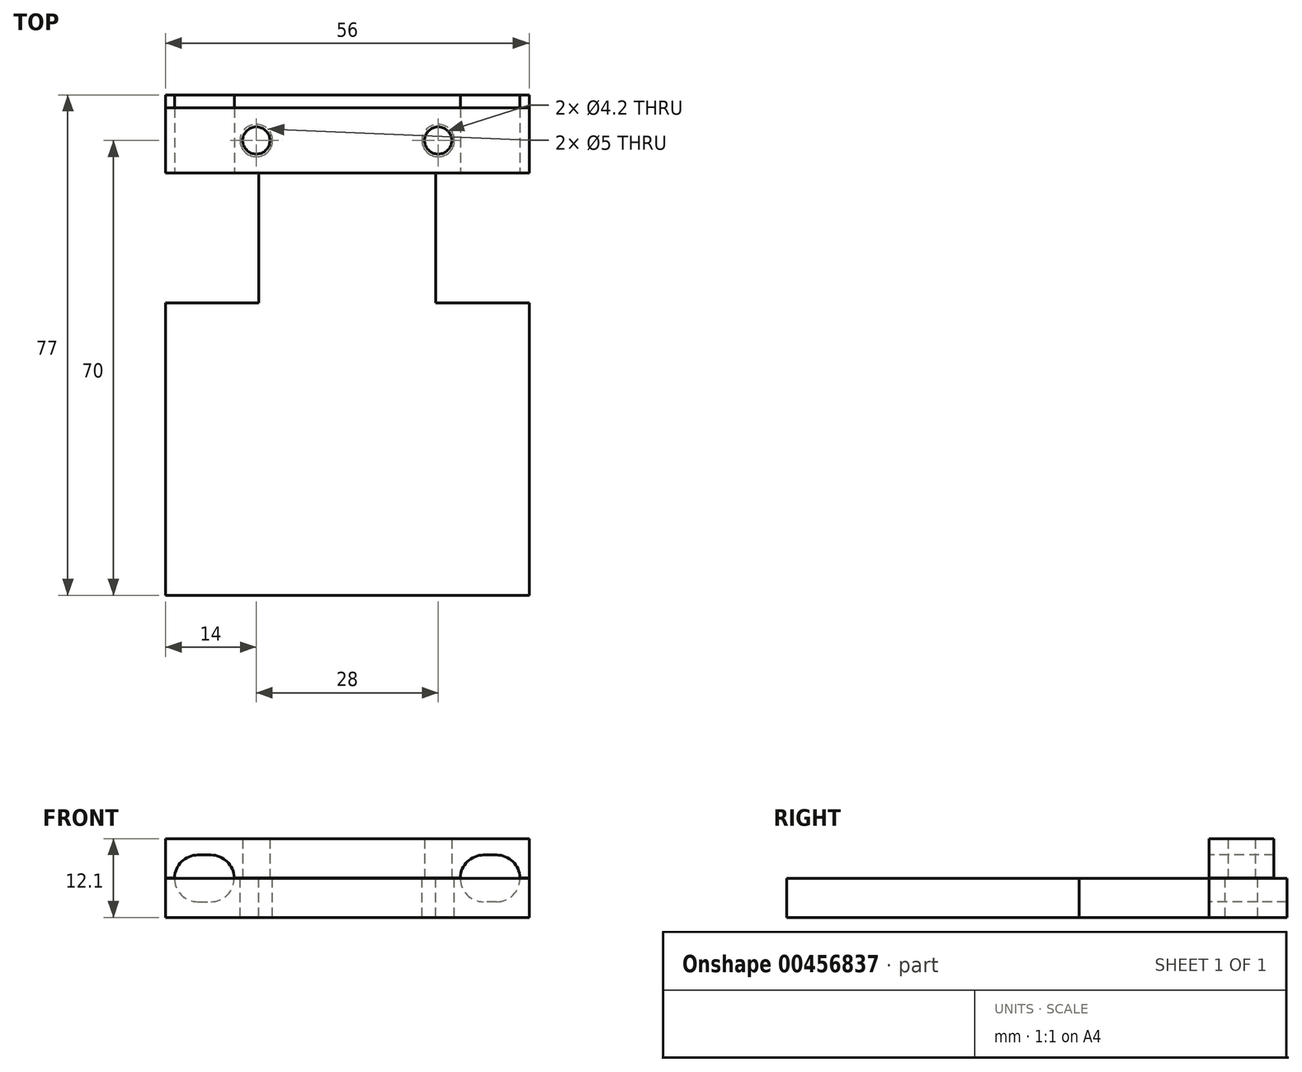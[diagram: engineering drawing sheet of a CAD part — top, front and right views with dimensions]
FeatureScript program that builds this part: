
annotation { "Feature Type Name" : "Feature", "Feature Type Description" : "" }
export const myFeature = defineFeature(function(context is Context, id is Id, definition is map)
    precondition{}
    {
        {
            var Q0;
            Q0=qCreatedBy(makeId("Front.planeOp"),FACE);
            var sketch = newSketch(context, id + "F0", { "sketchPlane" : qUnion([Q0])});
            skLineSegment(sketch, "E0", {"start": v(0, 0) * mm, "end": v(17.4, 0) * mm});
            skLineSegment(sketch, "E1", {"start": v(17.4, 0) * mm, "end": v(17.4, -6) * mm});
            skLineSegment(sketch, "E2", {"start": v(-17.4, -6) * mm, "end": v(-17.4, 0) * mm});
            skLineSegment(sketch, "E3", {"start": v(-17.4, 0) * mm, "end": v(0, 0) * mm});
            skCircle(sketch, "E4", {"center": v(21, 0) * mm, "radius": 3.6 * mm});
            skCircle(sketch, "E5", {"center": v(-21, 0) * mm, "radius": 3.6 * mm});
            skLineSegment(sketch, "E6", {"start": v(24.6, 0) * mm, "end": v(28, 0) * mm});
            skLineSegment(sketch, "E7", {"start": v(28, 0) * mm, "end": v(28, -6) * mm});
            skLineSegment(sketch, "E8", {"start": v(28, -6) * mm, "end": v(17.4, -6) * mm});
            skLineSegment(sketch, "E9", {"start": v(-24.6, 0) * mm, "end": v(-28, 0) * mm});
            skLineSegment(sketch, "E10", {"start": v(-28, 0) * mm, "end": v(-28, -6) * mm});
            skLineSegment(sketch, "E11", {"start": v(-28, -6) * mm, "end": v(-17.4, -6) * mm});
            skLineSegment(sketch, "E12", {"start": v(0, 0) * mm, "end": v(0, -6) * mm});
            skLineSegment(sketch, "E13", {"start": v(-28, 0) * mm, "end": v(-28, 6.1) * mm});
            skLineSegment(sketch, "E14", {"start": v(-28, 6.1) * mm, "end": v(28, 6.1) * mm});
            skLineSegment(sketch, "E15", {"start": v(28, 6.1) * mm, "end": v(28, 0) * mm});
            skLineSegment(sketch, "E16", {"start": v(-17.4, -6) * mm, "end": v(17.4, -6) * mm});
            skLineSegment(sketch, "E17", {"start": v(21, 0) * mm, "end": v(23, 0) * mm, "construction": true});
            skLineSegment(sketch, "E18", {"start": v(-21, 0) * mm, "end": v(-23, 0) * mm, "construction": true});
            skCircle(sketch, "E19", {"center": v(-23, 0) * mm, "radius": 3.6 * mm});
            skCircle(sketch, "E20", {"center": v(23, 0) * mm, "radius": 3.6 * mm});
            skLineSegment(sketch, "E21", {"start": v(-21, 3.6) * mm, "end": v(-23, 3.6) * mm});
            skLineSegment(sketch, "E22", {"start": v(-23, -3.6) * mm, "end": v(-21, -3.6) * mm});
            skLineSegment(sketch, "E23", {"start": v(23, 3.6) * mm, "end": v(21, 3.6) * mm});
            skLineSegment(sketch, "E24", {"start": v(23, -3.6) * mm, "end": v(21, -3.6) * mm});
            skLineSegment(sketch, "E25", {"start": v(-13.6, -6) * mm, "end": v(-13.6, 0) * mm});
            skLineSegment(sketch, "E26", {"start": v(13.6, -6) * mm, "end": v(13.6, 0) * mm});
            skPoint(sketch, "E27.orphan", {"position": v(13.6, -6) * mm});
            skLineSegment(sketch, "E28", {"start": v(-28, 0.1) * mm, "end": v(28, 0.1) * mm});
            skSolve(sketch);
        }
        {
            var Q0;
            {var subQ0=sQuery(id+"F0.wireOp",EDGE,"E0");Q0=makeQuery(id+"F0.imprint","IMPRINT",FACE,{"disambiguationData":[TD([[makeQuery(id+"F0.imprint","IMPRINT",EDGE,{"derivedFrom":subQ0}),-1.0]])]});}
            var Q1;
            {var subQ0=sQuery(id+"F0.wireOp",EDGE,"E3");Q1=makeQuery(id+"F0.imprint","IMPRINT",FACE,{"disambiguationData":[TD([[makeQuery(id+"F0.imprint","IMPRINT",EDGE,{"derivedFrom":subQ0}),-1.0]])]});}
            var Q2;
            {var subQ0=sQuery(id+"F0.wireOp",EDGE,"E10");Q2=makeQuery(id+"F0.imprint","IMPRINT",FACE,{"disambiguationData":[TD([[makeQuery(id+"F0.imprint","IMPRINT",EDGE,{"derivedFrom":subQ0}),1.0]])]});}
            var Q3;
            {var subQ0=sQuery(id+"F0.wireOp",EDGE,"E7");Q3=makeQuery(id+"F0.imprint","IMPRINT",FACE,{"disambiguationData":[TD([[makeQuery(id+"F0.imprint","IMPRINT",EDGE,{"derivedFrom":subQ0}),-1.0]])]});}
            extrude(context, id + "F1", {"entities" : qUnion([Q0, Q1, Q2, Q3]), "oppositeDirection" : true, "depth" : 12 * mm, "offsetDistance" : 25 * mm});
        }
        {
            var Q0;
            Q0=makeQuery(id+"F1.opExtrude","SWEPT_FACE",FACE,{"disambiguationData":[OSD([sQuery(id+"F0.wireOp",EDGE,"E0"),sQuery(id+"F0.wireOp",EDGE,"E3")])]});
            var sketch = newSketch(context, id + "F2", { "sketchPlane" : qUnion([Q0])});
            skLineSegment(sketch, "E29", {"start": v(0, -50) * mm, "end": v(0, 0) * mm, "construction": true});
            skCircle(sketch, "E30", {"center": v(0, -50) * mm, "radius": 13.6 * mm});
            skCircle(sketch, "E31", {"center": v(0, -50) * mm, "radius": 11 * mm});
            skLineSegment(sketch, "E32", {"start": v(0, -50) * mm, "end": v(0, -63.6) * mm, "construction": true});
            skPoint(sketch, "E33.orphan", {"position": v(0, -63.6) * mm});
            skLineSegment(sketch, "E34", {"start": v(-13.6, -50) * mm, "end": v(-13.6, 0) * mm});
            skLineSegment(sketch, "E35", {"start": v(-13.6, 0) * mm, "end": v(0, 0) * mm});
            skLineSegment(sketch, "E36", {"start": v(13.6, 0) * mm, "end": v(13.6, -50) * mm});
            skCircle(sketch, "E37", {"center": v(-6, -50) * mm, "radius": 2.5 * mm});
            skCircle(sketch, "E38", {"center": v(6, -50) * mm, "radius": 2.5 * mm});
            skCircle(sketch, "E39", {"center": v(-6, -50) * mm, "radius": 2.17 * mm});
            skCircle(sketch, "E40", {"center": v(6, -50) * mm, "radius": 2.17 * mm});
            skLineSegment(sketch, "E41.bottom", {"start": v(-9.6, -5) * mm, "end": v(-4.6, -5) * mm});
            skLineSegment(sketch, "E41.top", {"start": v(-9.6, -32.5) * mm, "end": v(-4.6, -32.5) * mm});
            skLineSegment(sketch, "E41.left", {"start": v(-9.6, -5) * mm, "end": v(-9.6, -32.5) * mm});
            skLineSegment(sketch, "E41.right", {"start": v(-4.6, -5) * mm, "end": v(-4.6, -32.5) * mm});
            skLineSegment(sketch, "E42.bottom", {"start": v(4.6, -5) * mm, "end": v(9.6, -5) * mm});
            skLineSegment(sketch, "E42.top", {"start": v(4.6, -32.5) * mm, "end": v(9.6, -32.5) * mm});
            skLineSegment(sketch, "E42.left", {"start": v(4.6, -5) * mm, "end": v(4.6, -32.5) * mm});
            skLineSegment(sketch, "E42.right", {"start": v(9.6, -5) * mm, "end": v(9.6, -32.5) * mm});
            skSolve(sketch);
        }
        {
            var Q0;
            Q0=qCreatedBy(makeId("Top.planeOp"),FACE);
            var sketch = newSketch(context, id + "F3", { "sketchPlane" : qUnion([Q0])});
            skLineSegment(sketch, "E43", {"start": v(0, 0) * mm, "end": v(0, 5) * mm, "construction": true});
            skLineSegment(sketch, "E44", {"start": v(0, 5) * mm, "end": v(14, 5) * mm, "construction": true});
            skLineSegment(sketch, "E45", {"start": v(0, 5) * mm, "end": v(-14, 5) * mm, "construction": true});
            skCircle(sketch, "E46", {"center": v(14, 5) * mm, "radius": 2.5 * mm});
            skCircle(sketch, "E47", {"center": v(-14, 5) * mm, "radius": 2.5 * mm});
            skCircle(sketch, "E48", {"center": v(-14, 5) * mm, "radius": 2.1 * mm});
            skCircle(sketch, "E49", {"center": v(14, 5) * mm, "radius": 2.1 * mm});
            skSolve(sketch);
        }
        {
            var Q0;
            {var subQ6=sQuery(id+"F0.wireOp",EDGE,"E14");Q0=makeQuery(id+"F0.imprint","IMPRINT",FACE,{"disambiguationData":[TD([[makeQuery(id+"F0.imprint","IMPRINT",EDGE,{"derivedFrom":subQ6}),-1.0]])]});}
            extrude(context, id + "F4", {"entities" : qUnion([Q0]), "oppositeDirection" : true, "depth" : 10 * mm, "offsetDistance" : 25 * mm});
        }
        {
            var Q0;
            Q0=makeQuery(id+"F3.imprint","IMPRINT",FACE,{"disambiguationData":[TD([[makeQuery(id+"F3.imprint","IMPRINT",EDGE,{"derivedFrom":sQuery(id+"F3.wireOp",EDGE,"E49")}),1.0]])]});
            var Q1;
            Q1=makeQuery(id+"F3.imprint","IMPRINT",FACE,{"disambiguationData":[TD([[makeQuery(id+"F3.imprint","IMPRINT",EDGE,{"derivedFrom":sQuery(id+"F3.wireOp",EDGE,"E48")}),1.0]])]});
            extrude(context, id + "F5", {"entities" : qUnion([Q0, Q1]), "operationType" : NewBodyOperationType.REMOVE, "depth" : 25 * mm, "offsetDistance" : 25 * mm});
        }
        {
            var Q0;
            Q0=makeQuery(id+"F3.imprint","IMPRINT",FACE,{"disambiguationData":[TD([[makeQuery(id+"F3.imprint","IMPRINT",EDGE,{"derivedFrom":sQuery(id+"F3.wireOp",EDGE,"E48")}),1.0]])]});
            var Q1;
            Q1=makeQuery(id+"F3.imprint","IMPRINT",FACE,{"disambiguationData":[TD([[makeQuery(id+"F3.imprint","IMPRINT",EDGE,{"derivedFrom":sQuery(id+"F3.wireOp",EDGE,"E47")}),1.0]])]});
            var Q2;
            Q2=makeQuery(id+"F3.imprint","IMPRINT",FACE,{"disambiguationData":[TD([[makeQuery(id+"F3.imprint","IMPRINT",EDGE,{"derivedFrom":sQuery(id+"F3.wireOp",EDGE,"E49")}),1.0]])]});
            var Q3;
            Q3=makeQuery(id+"F3.imprint","IMPRINT",FACE,{"disambiguationData":[TD([[makeQuery(id+"F3.imprint","IMPRINT",EDGE,{"derivedFrom":sQuery(id+"F3.wireOp",EDGE,"E46")}),1.0]])]});
            extrude(context, id + "F6", {"entities" : qUnion([Q0, Q1, Q2, Q3]), "operationType" : NewBodyOperationType.REMOVE, "oppositeDirection" : true, "depth" : 25 * mm, "offsetDistance" : 25 * mm});
        }
        {
            var Q0;
            {var subQ0=sQuery(id+"F2.wireOp",EDGE,"Ro7WqkXb-iyxD-nCUs-5sJY-u4c6l2cVIbbe");var subQ5=sQuery(id+"F2.wireOp",EDGE,"HMeDJbhX-BkRl-Xu3Z-KG4h-j2XgkNph2Sps");var subQ7=makeQuery(id+"F2.imprint","INTERSECT",VERTEX,{"derivedFrom":[subQ5,subQ0]});Q0=makeQuery(id+"F2.imprint","IMPRINT",FACE,{"disambiguationData":[TD([[makeQuery(id+"F2.imprint","IMPRINT",EDGE,{"disambiguationData":[TD([[subQ7,-1.0]])],"derivedFrom":subQ0}),-1.0]])]});}
            var Q1;
            {var subQ0=sQuery(id+"F2.wireOp",EDGE,"HMeDJbhX-BkRl-Xu3Z-KG4h-j2XgkNph2Sps");var subQ2=sQuery(id+"F0.wireOp",EDGE,"E0");var subQ4=makeQuery(id+"FEx8mM25Wbz40uY_2.opExtrude","CAP_EDGE",EDGE,{"disambiguationData":[OSD([subQ2,sQuery(id+"F0.wireOp",EDGE,"E3")])],"isStart":false});var subQ6=makeQuery(id+"F2.imprint","INTERSECT",VERTEX,{"derivedFrom":[subQ4,subQ0]});Q1=makeQuery(id+"F2.imprint","IMPRINT",FACE,{"disambiguationData":[TD([[makeQuery(id+"F2.imprint","IMPRINT",EDGE,{"disambiguationData":[TD([[subQ6,1.0]])],"derivedFrom":subQ4}),1.0]])]});}
            var Q2;
            {var subQ0=sQuery(id+"F2.wireOp",EDGE,"Ro7WqkXb-iyxD-nCUs-5sJY-u4c6l2cVIbbe");var subQ5=sQuery(id+"F2.wireOp",EDGE,"5ME1VgPx-wohn-Oeq3-YnMO-K018rfV1dcP1");var subQ6=makeQuery(id+"F2.imprint","INTERSECT",VERTEX,{"derivedFrom":[subQ0,subQ5]});Q2=makeQuery(id+"F2.imprint","IMPRINT",FACE,{"disambiguationData":[TD([[makeQuery(id+"F2.imprint","IMPRINT",EDGE,{"disambiguationData":[TD([[subQ6,1.0]])],"derivedFrom":subQ0}),-1.0]])]});}
            var Q3;
            {var subQ1=sQuery(id+"F2.wireOp",EDGE,"vZLtgpxl-h23v-mT7L-uQbk-GazwFbO4NxR9");var subQ2=sQuery(id+"F0.wireOp",EDGE,"E3");var subQ4=makeQuery(id+"FEx8mM25Wbz40uY_2.opExtrude","CAP_EDGE",EDGE,{"disambiguationData":[OSD([sQuery(id+"F0.wireOp",EDGE,"E0"),subQ2])],"isStart":false});var subQ5=makeQuery(id+"F2.imprint","INTERSECT",VERTEX,{"disambiguationData":[OD(0.0)],"derivedFrom":[subQ4,subQ1]});Q3=makeQuery(id+"F2.imprint","IMPRINT",FACE,{"disambiguationData":[TD([[makeQuery(id+"F2.imprint","IMPRINT",EDGE,{"disambiguationData":[TD([[subQ5,1.0]])],"derivedFrom":subQ1}),-1.0]])]});}
            var Q4;
            {var subQ0=sQuery(id+"F2.wireOp",EDGE,"E31");var subQ1=makeQuery(id+"F2.imprint","INTERSECT",VERTEX,{"derivedFrom":[subQ0,sQuery(id+"F2.wireOp",EDGE,"MiQvAYG1-QENy-Oij3-06Sa-qeLXIY0G7tAl")]});Q4=makeQuery(id+"F2.imprint","IMPRINT",FACE,{"disambiguationData":[TD([[makeQuery(id+"F2.imprint","IMPRINT",EDGE,{"disambiguationData":[TD([[subQ1,-1.0]])],"derivedFrom":subQ0}),1.0]])]});}
            var Q5;
            {var subQ0=sQuery(id+"F2.wireOp",EDGE,"MiQvAYG1-QENy-Oij3-06Sa-qeLXIY0G7tAl");var subQ5=sQuery(id+"F2.wireOp",EDGE,"E31");var subQ6=makeQuery(id+"F2.imprint","INTERSECT",VERTEX,{"derivedFrom":[subQ5,subQ0]});Q5=makeQuery(id+"F2.imprint","IMPRINT",FACE,{"disambiguationData":[TD([[makeQuery(id+"F2.imprint","IMPRINT",EDGE,{"disambiguationData":[TD([[subQ6,-1.0]])],"derivedFrom":subQ0}),1.0]])]});}
            var Q6;
            {var subQ0=sQuery(id+"F2.wireOp",EDGE,"E30");var subQ1=makeQuery(id+"FEx8mM25Wbz40uY_2.opExtrude","CAP_EDGE",EDGE,{"disambiguationData":[OSD([sQuery(id+"F0.wireOp",EDGE,"E0"),sQuery(id+"F0.wireOp",EDGE,"E3")])],"isStart":false});var subQ2=makeQuery(id+"F2.imprint","INTERSECT",VERTEX,{"disambiguationData":[OD(0.0)],"derivedFrom":[subQ1,subQ0]});Q6=makeQuery(id+"F2.imprint","IMPRINT",FACE,{"disambiguationData":[TD([[makeQuery(id+"F2.imprint","IMPRINT",EDGE,{"disambiguationData":[TD([[subQ2,-1.0]])],"derivedFrom":subQ0}),1.0]])]});}
            var Q7;
            {var subQ0=sQuery(id+"F2.wireOp",EDGE,"MiQvAYG1-QENy-Oij3-06Sa-qeLXIY0G7tAl");var subQ5=sQuery(id+"F2.wireOp",EDGE,"E31");var subQ6=makeQuery(id+"F2.imprint","INTERSECT",VERTEX,{"derivedFrom":[subQ5,subQ0]});Q7=makeQuery(id+"F2.imprint","IMPRINT",FACE,{"disambiguationData":[TD([[makeQuery(id+"F2.imprint","IMPRINT",EDGE,{"disambiguationData":[TD([[subQ6,-1.0]])],"derivedFrom":subQ0}),-1.0]])]});}
            extrude(context, id + "F7", {"entities" : qUnion([Q0, Q1, Q2, Q3, Q4, Q5, Q6, Q7]), "operationType" : NewBodyOperationType.REMOVE, "oppositeDirection" : true, "depth" : 25 * mm, "offsetDistance" : 25 * mm});
        }
        {
            var Q0;
            {var subQ0=sQuery(id+"F0.wireOp",EDGE,"E12");Q0=makeQuery(id+"F0.imprint","IMPRINT",FACE,{"disambiguationData":[TD([[makeQuery(id+"F0.imprint","IMPRINT",EDGE,{"derivedFrom":subQ0}),-1.0]])]});}
            var Q1;
            {var subQ0=sQuery(id+"F0.wireOp",EDGE,"E12");Q1=makeQuery(id+"F0.imprint","IMPRINT",FACE,{"disambiguationData":[TD([[makeQuery(id+"F0.imprint","IMPRINT",EDGE,{"derivedFrom":subQ0}),1.0]])]});}
            extrude(context, id + "F8", {"entities" : qUnion([Q0, Q1]), "operationType" : NewBodyOperationType.ADD, "depth" : 65 * mm, "offsetDistance" : 25 * mm});
        }
        {
            var Q0;
            {var subQ0=sQuery(id+"F0.wireOp",EDGE,"E3");var subQ1=sQuery(id+"F0.wireOp",EDGE,"E0");Q0=makeQuery(id+"F8.boolean.opBoolean","MERGE",FACE,{"derivedFrom":[makeQuery(id+"F1.opExtrude","SWEPT_FACE",FACE,{"disambiguationData":[OSD([subQ1,subQ0])]}),makeQuery(id+"F8.opExtrude","SWEPT_FACE",FACE,{"disambiguationData":[OSD([subQ1,subQ0])]})]});}
            var sketch = newSketch(context, id + "F9", { "sketchPlane" : qUnion([Q0])});
            skLineSegment(sketch, "E50.bottom", {"start": v(-13.6, -65) * mm, "end": v(-28, -65) * mm});
            skLineSegment(sketch, "E50.top", {"start": v(-13.6, -20) * mm, "end": v(-28, -20) * mm});
            skLineSegment(sketch, "E50.left", {"start": v(-13.6, -65) * mm, "end": v(-13.6, -20) * mm});
            skLineSegment(sketch, "E50.right", {"start": v(-28, -65) * mm, "end": v(-28, -20) * mm});
            skLineSegment(sketch, "E51.bottom", {"start": v(13.6, -65) * mm, "end": v(28, -65) * mm});
            skLineSegment(sketch, "E51.top", {"start": v(13.6, -20) * mm, "end": v(28, -20) * mm});
            skLineSegment(sketch, "E51.left", {"start": v(13.6, -65) * mm, "end": v(13.6, -20) * mm});
            skLineSegment(sketch, "E51.right", {"start": v(28, -65) * mm, "end": v(28, -20) * mm});
            skSolve(sketch);
        }
        {
            var Q0;
            Q0=makeQuery(id+"F9.imprint","IMPRINT",FACE,{"disambiguationData":[TD([[makeQuery(id+"F9.imprint","IMPRINT",EDGE,{"derivedFrom":sQuery(id+"F9.wireOp",EDGE,"E50.bottom")}),-1.0]])]});
            var Q1;
            Q1=makeQuery(id+"F9.imprint","IMPRINT",FACE,{"disambiguationData":[TD([[makeQuery(id+"F9.imprint","IMPRINT",EDGE,{"derivedFrom":sQuery(id+"F9.wireOp",EDGE,"E51.bottom")}),1.0]])]});
            extrude(context, id + "F10", {"entities" : qUnion([Q0, Q1]), "operationType" : NewBodyOperationType.ADD, "oppositeDirection" : true, "depth" : 6 * mm, "offsetDistance" : 25 * mm});
        }
    });
